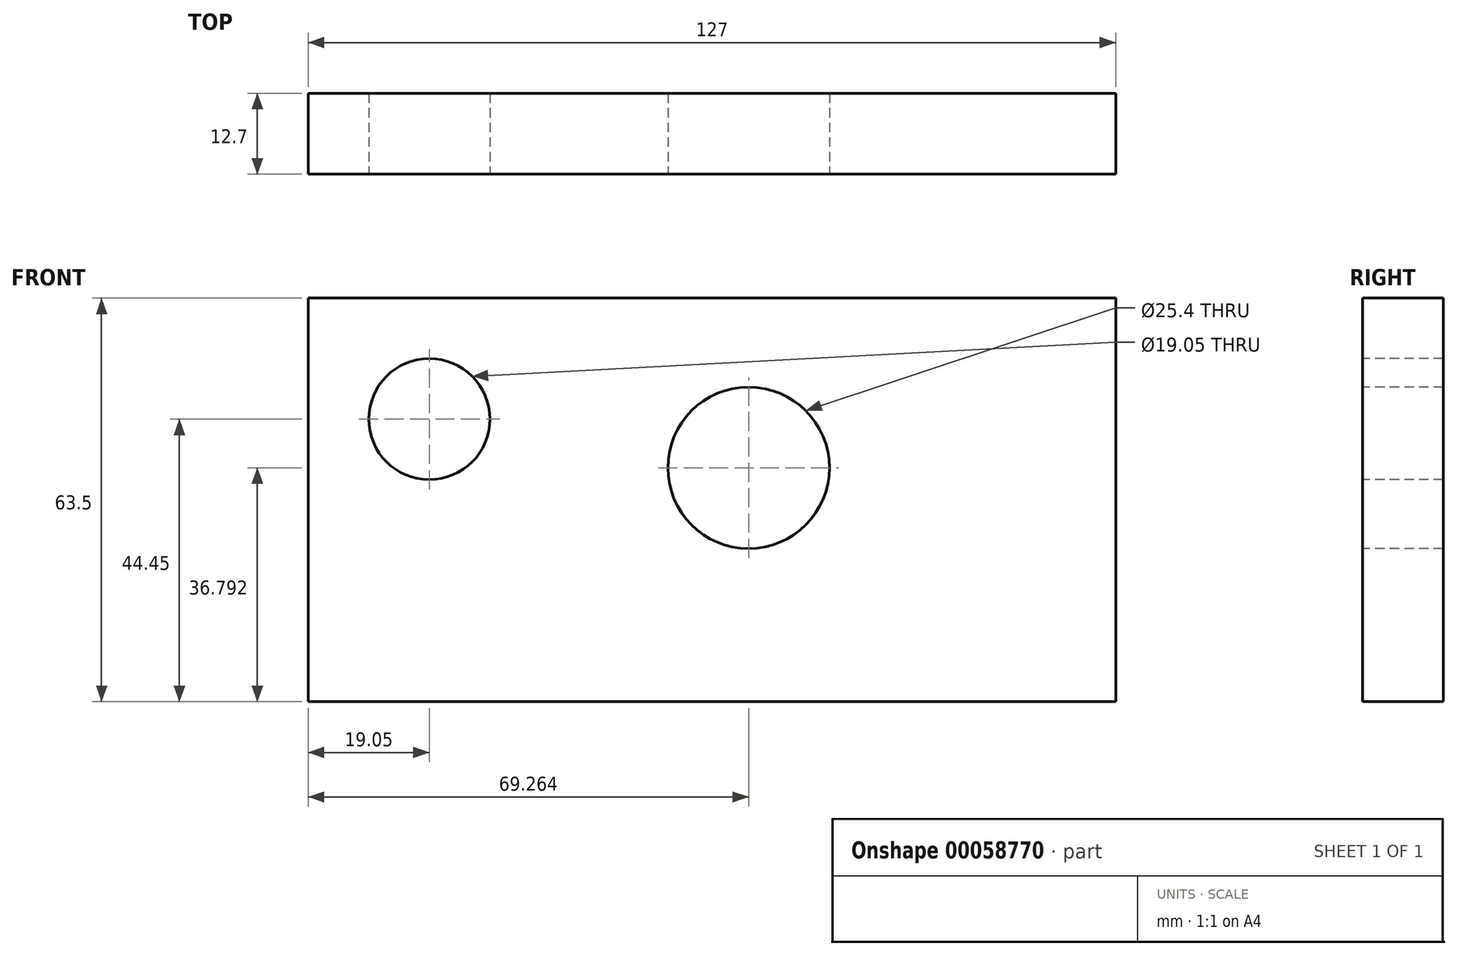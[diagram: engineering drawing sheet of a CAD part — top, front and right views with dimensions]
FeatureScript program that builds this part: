
annotation { "Feature Type Name" : "Feature", "Feature Type Description" : "" }
export const myFeature = defineFeature(function(context is Context, id is Id, definition is map)
    precondition{}
    {
        {
            var Q0;
            Q0=qCreatedBy(makeId("Front.planeOp"),FACE);
            var sketch = newSketch(context, id + "F0", { "sketchPlane" : qUnion([Q0])});
            skLineSegment(sketch, "E0.bottom", {"start": v(0, 0) * mm, "end": v(127, 0) * mm});
            skLineSegment(sketch, "E0.top", {"start": v(0, 63.5) * mm, "end": v(127, 63.5) * mm});
            skLineSegment(sketch, "E0.left", {"start": v(0, 0) * mm, "end": v(0, 63.5) * mm});
            skLineSegment(sketch, "E0.right", {"start": v(127, 0) * mm, "end": v(127, 63.5) * mm});
            skSolve(sketch);
        }
        {
            var Q0;
            Q0 = qSketchRegion(id + "F0", true);
            extrude(context, id + "F1", {"entities" : qUnion([Q0]), "depth" : 12.7 * mm});
        }
        {
            var Q0;
            Q0=makeQuery(id+"F1.opExtrude","CAP_FACE",FACE,{"disambiguationData":[OSD([sQuery(id+"F0.wireOp",EDGE,"E0.bottom"),sQuery(id+"F0.wireOp",EDGE,"E0.top"),sQuery(id+"F0.wireOp",EDGE,"E0.left"),sQuery(id+"F0.wireOp",EDGE,"E0.right")])],"isStart":false});
            var sketch = newSketch(context, id + "F2", { "sketchPlane" : qUnion([Q0])});
            skCircle(sketch, "E1", {"center": v(19.05, 44.45) * mm, "radius": 9.53 * mm});
            skCircle(sketch, "E2", {"center": v(69.26, 36.8) * mm, "radius": 12.7 * mm});
            skLineSegment(sketch, "E3", {"start": v(19.05, 44.45) * mm, "end": v(19.05, 63.5) * mm, "construction": true});
            skLineSegment(sketch, "E4", {"start": v(19.05, 44.45) * mm, "end": v(0, 44.45) * mm, "construction": true});
            skSolve(sketch);
        }
        {
            var Q0;
            Q0 = qSketchRegion(id + "F2", true);
            extrude(context, id + "F3", {"entities" : qUnion([Q0]), "operationType" : NewBodyOperationType.REMOVE, "endBound" : BoundingType.THROUGH_ALL, "oppositeDirection" : true, "depth" : 25.4 * mm});
        }
    });
